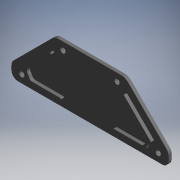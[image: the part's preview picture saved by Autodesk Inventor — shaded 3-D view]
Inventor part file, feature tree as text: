
AUTODESK INVENTOR PART (.ipt)
format: ipt  version: 2017.3 (Build 213256000, 256)  size: 148,480 bytes
history: native  units: mm (DEFAULTED — no unit token found)
features: other x14, extrude x3, sketch x3
ambient origin geometry x8: Origin, YZ Plane, XZ Plane, XY Plane, X Axis, Y Axis, Z Axis, Center Point
bodies: Solid1 (feature_tree)
feature tree (20):
  extrude  "Extrusion1"  Depth=3.2mm TaperAngle=0.0deg
  extrude  "Extrusion2"  TaperAngle=0.0deg  [1 undecoded]
  extrude  "Extrusion3"  [1 undecoded]
  other  "swivel_to_body_XY"
  other  "swivel_to_body_YZ"
  other  "swivel_to_body_ZX"
  other  "swivel_to_body_X"
  other  "swivel_to_body_Y"
  other  "swivel_to_body_Z"
  other  "swivel_to_body_Center"
  other  "swivel_to_dummy_XY"
  other  "swivel_to_dummy_YZ"
  other  "swivel_to_dummy_ZX"
  other  "swivel_to_dummy_X"
  other  "swivel_to_dummy_Y"
  other  "swivel_to_dummy_Z"
  other  "swivel_to_dummy_Center"
  sketch  "Sketch_1"  dims[d0=3.2mm d1=0.0mm d2=3.2mm d3=0.0mm]
  sketch  "Sketch_2"  dims[d4=3.2mm d5=0.0mm d6=0.0mm]
  sketch  "Sketch_3"
note: 2 required parameter values undecoded (feature->parameter linkage not recoverable at this tier; creation-order binding heuristic only, values carry confidence <= 0.55)
